# Revit family: 400_ISR_PGAII_waterdicht_opbouwarmatuur
name_source: partatom
category: Lighting Fixtures
revit_build: Autodesk Revit 2013 (Build: 20121003_2115(x64)
units: mm (PartAtom-declared; Revit-internal decimal feet)

## types (6) — shared parameters
Apparent Load = 0 VA
Color Filter = 16777215
Description = PGAII
Dimming Lamp Color Temperature Shift = <None>
Emit from Line Length = 610 mm
Lamp = T8
Load Classification = Other
Manufacturer = Lightronics
Model = LOD400
Photometric Web File = PGA-T8-1-36-X-E-H-X-230-X-W.ies
Tilt Angle = 90.00°
URL = http://www.lightronics.nl

## per-type parameters (varying)
| type | 1x | 2x | A | L | Wattage Comments |
| 1x18 Watt | Yes | No | 390 mm  [stored 1.27953 ft] | 660 mm | 1 x 18 Watt |
| 1x36 Watt | Yes | No | 800 mm  [stored 2.62467 ft] | 1277 mm  [stored 4.18963 ft] | 1 x 36 Watt |
| 1x58 Watt | Yes | No | 1100 mm | 1573 mm  [stored 5.16076 ft] | 1 x 58 Watt |
| 2x18 Watt | No | Yes | 390 mm  [stored 1.27953 ft] | 660 mm | 2 x 18 Watt |
| 2x36 Watt | No | Yes | 800 mm  [stored 2.62467 ft] | 1277 mm  [stored 4.18963 ft] | 2 x 36 Watt |
| 2x58 Watt | No | Yes | 1100 mm | 1573 mm  [stored 5.16076 ft] | 2 x 58 Watt |

note: [stored X ft] marks values corroborated as IEEE doubles in the binary element streams (Revit-internal decimal feet)

## geometry (parser evidence)
native form markers: Sweep x1
no freeform markers — native parametric forms only
